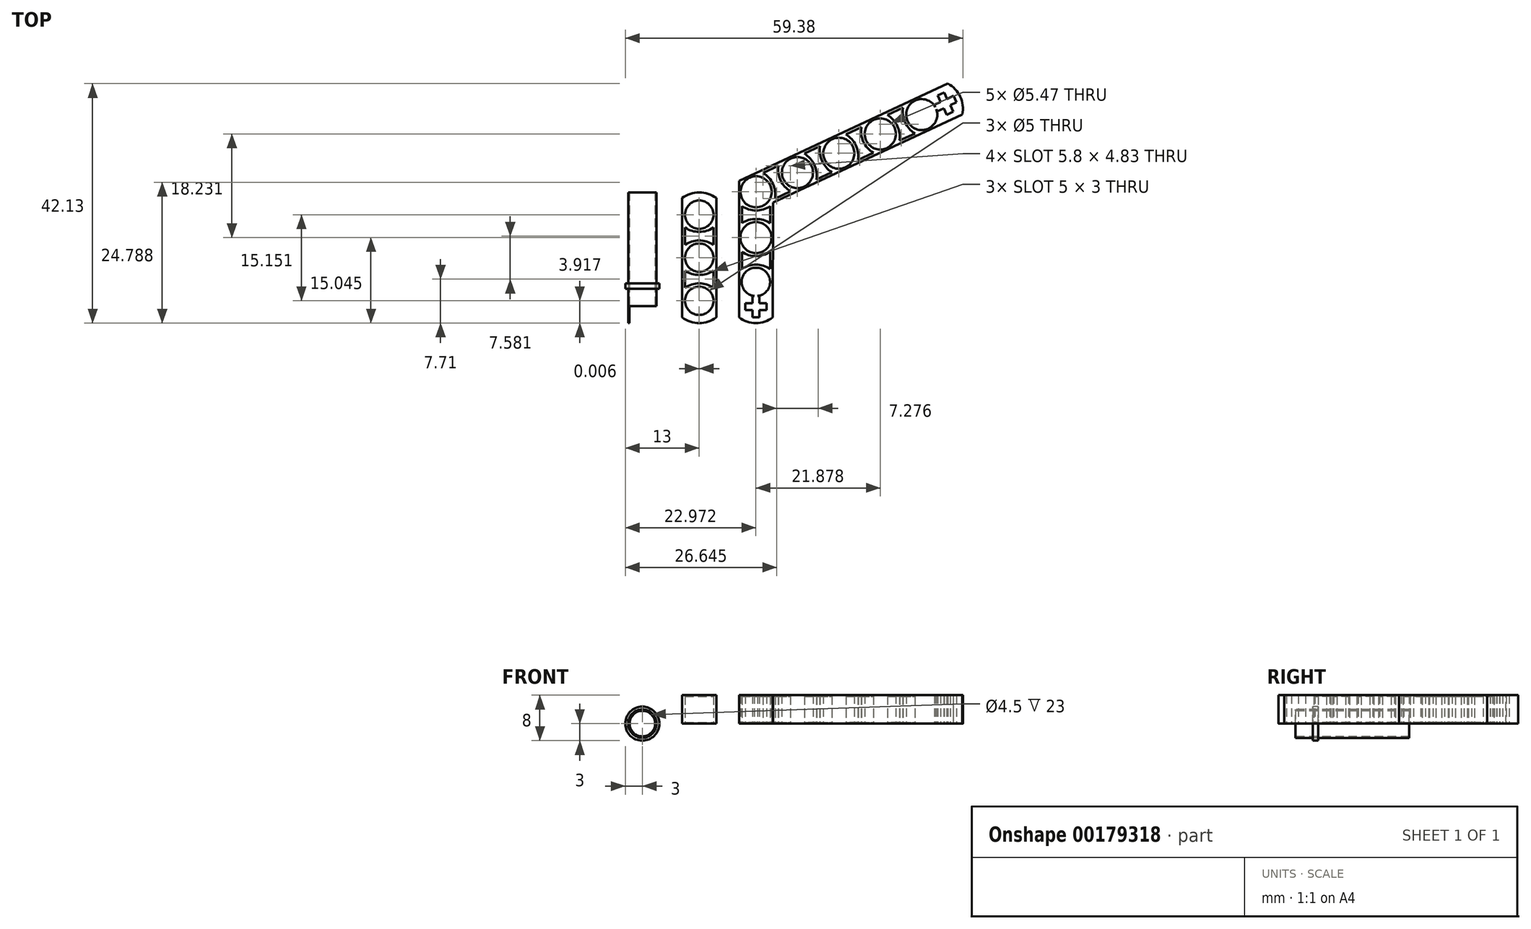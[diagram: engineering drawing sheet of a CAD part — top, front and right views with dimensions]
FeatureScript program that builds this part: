
annotation { "Feature Type Name" : "Feature", "Feature Type Description" : "" }
export const myFeature = defineFeature(function(context is Context, id is Id, definition is map)
    precondition{}
    {
        {
            var Q0;
            Q0=qCreatedBy(makeId("Top.planeOp"),FACE);
            var sketch = newSketch(context, id + "F0", { "sketchPlane" : qUnion([Q0])});
            skLineSegment(sketch, "E0", {"start": v(0, 1) * mm, "end": v(0, 23) * mm});
            skLineSegment(sketch, "E1", {"start": v(6, 22) * mm, "end": v(6, 1) * mm});
            skCircle(sketch, "E2", {"center": v(3, 11.5) * mm, "radius": 2.5 * mm});
            skLineSegment(sketch, "E3", {"start": v(0.5, 15.3) * mm, "end": v(0, 15.3) * mm, "construction": true});
            skLineSegment(sketch, "E4", {"start": v(3.02, 15.3) * mm, "end": v(6, 15.3) * mm, "construction": true});
            skLineSegment(sketch, "E5", {"start": v(0, 15.3) * mm, "end": v(0, 16.8) * mm, "construction": true});
            skLineSegment(sketch, "E6", {"start": v(0, 16.8) * mm, "end": v(0.5, 16.8) * mm, "construction": true});
            skLineSegment(sketch, "E7", {"start": v(0, 15.3) * mm, "end": v(0, 13.8) * mm, "construction": true});
            skLineSegment(sketch, "E8", {"start": v(0, 13.8) * mm, "end": v(0.5, 13.8) * mm, "construction": true});
            skLineSegment(sketch, "E9", {"start": v(6, 15.3) * mm, "end": v(6, 16.8) * mm});
            skLineSegment(sketch, "E10", {"start": v(6, 16.8) * mm, "end": v(5.5, 16.8) * mm, "construction": true});
            skLineSegment(sketch, "E11", {"start": v(6, 15.3) * mm, "end": v(6, 13.8) * mm, "construction": true});
            skLineSegment(sketch, "E12", {"start": v(6, 13.8) * mm, "end": v(5.5, 13.8) * mm, "construction": true});
            skLineSegment(sketch, "E13", {"start": v(6, 15.3) * mm, "end": v(6, 16.8) * mm, "construction": true});
            skLineSegment(sketch, "E14", {"start": v(0.5, 16.8) * mm, "end": v(0.5, 13.8) * mm});
            skLineSegment(sketch, "E15", {"start": v(5.5, 16.8) * mm, "end": v(5.5, 13.8) * mm});
            skLineSegment(sketch, "E16", {"start": v(6, 16.04) * mm, "end": v(0, 16.04) * mm, "construction": true});
            skLineSegment(sketch, "E17", {"start": v(6, 14.54) * mm, "end": v(0, 14.54) * mm, "construction": true});
            skArc(sketch, "E18", {"start": v(0.5, 16.8) * mm, "mid": v(3, 16.04) * mm, "end": v(5.5, 16.8) * mm});
            skArc(sketch, "E19", {"start": v(5.5, 13.8) * mm, "mid": v(3, 14.54) * mm, "end": v(0.5, 13.8) * mm});
            skPoint(sketch, "E20.endSnap0", {"position": v(3, 7.7) * mm});
            skLineSegment(sketch, "E21", {"start": v(3, 7.7) * mm, "end": v(6, 7.7) * mm, "construction": true});
            skLineSegment(sketch, "E22", {"start": v(0, 7.7) * mm, "end": v(0, 6.2) * mm, "construction": true});
            skLineSegment(sketch, "E23", {"start": v(0, 7.7) * mm, "end": v(0, 9.2) * mm, "construction": true});
            skLineSegment(sketch, "E24", {"start": v(6, 7.7) * mm, "end": v(6, 9.2) * mm, "construction": true});
            skLineSegment(sketch, "E25", {"start": v(6, 7.7) * mm, "end": v(6, 6.2) * mm, "construction": true});
            skLineSegment(sketch, "E26", {"start": v(6, 6.96) * mm, "end": v(0, 6.96) * mm, "construction": true});
            skLineSegment(sketch, "E27", {"start": v(0, 8.46) * mm, "end": v(6, 8.46) * mm, "construction": true});
            skLineSegment(sketch, "E28", {"start": v(6, 9.2) * mm, "end": v(5.5, 9.2) * mm, "construction": true});
            skLineSegment(sketch, "E29", {"start": v(0, 9.2) * mm, "end": v(0.5, 9.2) * mm, "construction": true});
            skLineSegment(sketch, "E30", {"start": v(0, 6.2) * mm, "end": v(0.5, 6.2) * mm, "construction": true});
            skLineSegment(sketch, "E31", {"start": v(6, 6.2) * mm, "end": v(5.5, 6.2) * mm, "construction": true});
            skArc(sketch, "E32", {"start": v(0.5, 9.2) * mm, "mid": v(3, 8.46) * mm, "end": v(5.5, 9.2) * mm});
            skArc(sketch, "E33", {"start": v(5.5, 6.2) * mm, "mid": v(3, 6.96) * mm, "end": v(0.5, 6.2) * mm});
            skLineSegment(sketch, "E34", {"start": v(5.5, 9.2) * mm, "end": v(5.5, 6.2) * mm});
            skLineSegment(sketch, "E35", {"start": v(0.5, 9.2) * mm, "end": v(0.5, 6.2) * mm});
            skLineSegment(sketch, "E36", {"start": v(3, 23) * mm, "end": v(3, 21) * mm, "construction": true});
            skLineSegment(sketch, "E37", {"start": v(3, 22) * mm, "end": v(6, 22) * mm, "construction": true});
            skLineSegment(sketch, "E38", {"start": v(3, 22) * mm, "end": v(0, 22) * mm, "construction": true});
            skArc(sketch, "E39", {"start": v(6, 22) * mm, "mid": v(3, 23) * mm, "end": v(0, 22) * mm});
            skPoint(sketch, "E40.orphan", {"position": v(6, 23) * mm});
            skLineSegment(sketch, "E41", {"start": v(3, 0) * mm, "end": v(3, 2) * mm, "construction": true});
            skLineSegment(sketch, "E42", {"start": v(3, 1) * mm, "end": v(6, 1) * mm, "construction": true});
            skLineSegment(sketch, "E43", {"start": v(3, 1) * mm, "end": v(0, 1) * mm, "construction": true});
            skArc(sketch, "E44", {"start": v(0, 1) * mm, "mid": v(3, 0) * mm, "end": v(6, 1) * mm});
            skPoint(sketch, "E45.orphan", {"position": v(6, 0) * mm});
            skPoint(sketch, "E46.orphan", {"position": v(0, 0) * mm});
            skLineSegment(sketch, "E47", {"start": v(3, 2) * mm, "end": v(3, 5) * mm, "construction": true});
            skCircle(sketch, "E48", {"center": v(3, 3.92) * mm, "radius": 2.5 * mm});
            skLineSegment(sketch, "E49", {"start": v(3, 6.42) * mm, "end": v(3, 9) * mm, "construction": true});
            skLineSegment(sketch, "E50", {"start": v(3, 7.7) * mm, "end": v(0, 7.7) * mm, "construction": true});
            skCircle(sketch, "E51", {"center": v(3, 19.07) * mm, "radius": 2.5 * mm});
            skLineSegment(sketch, "E52", {"start": v(3.02, 15.3) * mm, "end": v(3.02, 16.57) * mm, "construction": true});
            skLineSegment(sketch, "E53", {"start": v(3.02, 15.3) * mm, "end": v(3.02, 14) * mm, "construction": true});
            skLineSegment(sketch, "E54", {"start": v(3.02, 14) * mm, "end": v(3.02, 16.57) * mm, "construction": true});
            skPoint(sketch, "E55.start.orphan", {"position": v(3.02, 15.28) * mm});
            skLineSegment(sketch, "E56", {"start": v(3.02, 15.3) * mm, "end": v(0.5, 15.3) * mm, "construction": true});
            skLineSegment(sketch, "E57", {"start": v(0, 0) * mm, "end": v(-7, 0) * mm, "construction": true});
            skSolve(sketch);
        }
        {
            var Q0;
            Q0 = qSketchRegion(id + "F0", true);
            extrude(context, id + "F1", {"entities" : qUnion([Q0]), "depth" : 5 * mm});
        }
        {
            var Q0;
            Q0=makeQuery(id+"F0.imprint","IMPRINT",FACE,{"disambiguationData":[TD([[makeQuery(id+"F0.imprint","IMPRINT",EDGE,{"derivedFrom":sQuery(id+"F0.wireOp",EDGE,"E14")}),1.0]])]});
            var Q1;
            Q1=makeQuery(id+"F0.imprint","IMPRINT",FACE,{"disambiguationData":[TD([[makeQuery(id+"F0.imprint","IMPRINT",EDGE,{"derivedFrom":sQuery(id+"F0.wireOp",EDGE,"E32")}),-1.0]])]});
            extrude(context, id + "F2", {"entities" : qUnion([Q0, Q1]), "depth" : 5 * mm});
        }
        {
            var Q0;
            Q0=makeQuery(id+"F2.opExtrude","CAP_FACE",FACE,{"disambiguationData":[OSD([sQuery(id+"F0.wireOp",EDGE,"E14"),sQuery(id+"F0.wireOp",EDGE,"E15"),sQuery(id+"F0.wireOp",EDGE,"E18"),sQuery(id+"F0.wireOp",EDGE,"E19")])],"isStart":true});
            extrude(context, id + "F3", {"entities" : qUnion([Q0]), "operationType" : NewBodyOperationType.REMOVE, "oppositeDirection" : true, "depth" : 0.2 * mm});
        }
        {
            var Q0;
            Q0=makeQuery(id+"F2.opExtrude","CAP_FACE",FACE,{"disambiguationData":[OSD([sQuery(id+"F0.wireOp",EDGE,"E14"),sQuery(id+"F0.wireOp",EDGE,"E15"),sQuery(id+"F0.wireOp",EDGE,"E18"),sQuery(id+"F0.wireOp",EDGE,"E19")])],"isStart":false});
            extrude(context, id + "F4", {"entities" : qUnion([Q0]), "operationType" : NewBodyOperationType.REMOVE, "oppositeDirection" : true, "depth" : 0.2 * mm});
        }
        {
            var Q0;
            Q0=makeQuery(id+"F2.opExtrude","CAP_FACE",FACE,{"disambiguationData":[OSD([sQuery(id+"F0.wireOp",EDGE,"E32"),sQuery(id+"F0.wireOp",EDGE,"E33"),sQuery(id+"F0.wireOp",EDGE,"E34"),sQuery(id+"F0.wireOp",EDGE,"E35")])],"isStart":true});
            extrude(context, id + "F5", {"entities" : qUnion([Q0]), "operationType" : NewBodyOperationType.REMOVE, "oppositeDirection" : true, "depth" : 0.2 * mm});
        }
        {
            var Q0;
            Q0=makeQuery(id+"F2.opExtrude","CAP_FACE",FACE,{"disambiguationData":[OSD([sQuery(id+"F0.wireOp",EDGE,"E32"),sQuery(id+"F0.wireOp",EDGE,"E33"),sQuery(id+"F0.wireOp",EDGE,"E34"),sQuery(id+"F0.wireOp",EDGE,"E35")])],"isStart":false});
            extrude(context, id + "F6", {"entities" : qUnion([Q0]), "operationType" : NewBodyOperationType.REMOVE, "oppositeDirection" : true, "depth" : 0.2 * mm});
        }
        {
            var Q0;
            Q0=qCreatedBy(makeId("Top.planeOp"),FACE);
            var sketch = newSketch(context, id + "F7", { "sketchPlane" : qUnion([Q0])});
            skLineSegment(sketch, "E58", {"start": v(0, 0) * mm, "end": v(10, 0) * mm, "construction": true});
            skLineSegment(sketch, "E59", {"start": v(10, 1) * mm, "end": v(10, 25) * mm});
            skLineSegment(sketch, "E60", {"start": v(10, 25) * mm, "end": v(46.74, 42.13) * mm});
            skLineSegment(sketch, "E61", {"start": v(10, 25) * mm, "end": v(16, 21.18) * mm, "construction": true});
            skLineSegment(sketch, "E62", {"start": v(10, 21.18) * mm, "end": v(16, 21.18) * mm, "construction": true});
            skLineSegment(sketch, "E63", {"start": v(49.28, 36.7) * mm, "end": v(16, 21.18) * mm});
            skLineSegment(sketch, "E64", {"start": v(15.95, 1) * mm, "end": v(16, 21.18) * mm});
            skCircle(sketch, "E65", {"center": v(13, 23.09) * mm, "radius": 2.73 * mm});
            skLineSegment(sketch, "E66", {"start": v(12.97, 1) * mm, "end": v(12.97, 9.74) * mm, "construction": true});
            skLineSegment(sketch, "E67", {"start": v(12.97, 5.09) * mm, "end": v(12.97, 7.24) * mm, "construction": true});
            skCircle(sketch, "E68", {"center": v(12.97, 7.24) * mm, "radius": 2.5 * mm});
            skLineSegment(sketch, "E69", {"start": v(20.29, 26.49) * mm, "end": v(20.29, 26.5) * mm, "construction": true});
            skArc(sketch, "E70", {"start": v(20.29, 26.49) * mm, "mid": v(20.29, 26.49) * mm, "end": v(20.29, 26.5) * mm});
            skArc(sketch, "E71", {"start": v(10, 1) * mm, "mid": v(12.97, 0) * mm, "end": v(15.95, 1) * mm});
            skPoint(sketch, "E72.start.orphan", {"position": v(15.94, 0) * mm});
            skLineSegment(sketch, "E73", {"start": v(12.35, 1) * mm, "end": v(12.97, 1) * mm, "construction": true});
            skLineSegment(sketch, "E74", {"start": v(12.97, 1) * mm, "end": v(12.35, 1) * mm});
            skLineSegment(sketch, "E75", {"start": v(12.97, 1) * mm, "end": v(13.6, 1) * mm});
            skLineSegment(sketch, "E76", {"start": v(13.6, 1) * mm, "end": v(13.6, 2.25) * mm});
            skLineSegment(sketch, "E77", {"start": v(13.6, 2.25) * mm, "end": v(14.85, 2.25) * mm});
            skLineSegment(sketch, "E78", {"start": v(14.85, 2.25) * mm, "end": v(14.85, 3.5) * mm});
            skLineSegment(sketch, "E79", {"start": v(14.85, 3.5) * mm, "end": v(13.6, 3.5) * mm});
            skLineSegment(sketch, "E80", {"start": v(12.35, 2.25) * mm, "end": v(12.35, 1) * mm});
            skLineSegment(sketch, "E81", {"start": v(13.6, 3.5) * mm, "end": v(13.6, 4.75) * mm});
            skLineSegment(sketch, "E82", {"start": v(13.6, 4.75) * mm, "end": v(12.35, 4.75) * mm});
            skLineSegment(sketch, "E83", {"start": v(12.35, 4.75) * mm, "end": v(12.35, 3.5) * mm});
            skLineSegment(sketch, "E84", {"start": v(12.35, 3.5) * mm, "end": v(11.1, 3.5) * mm});
            skLineSegment(sketch, "E85", {"start": v(11.1, 3.5) * mm, "end": v(11.1, 2.25) * mm});
            skLineSegment(sketch, "E86", {"start": v(11.1, 2.25) * mm, "end": v(12.35, 2.25) * mm});
            skLineSegment(sketch, "E87.trimOffspring", {"start": v(12.97, 18.35) * mm, "end": v(12.97, 18.35) * mm, "construction": true});
            skPoint(sketch, "E88.orphan", {"position": v(12.97, 20.36) * mm});
            skPoint(sketch, "E89.orphan", {"position": v(12.97, 10.18) * mm});
            skLineSegment(sketch, "E90", {"start": v(12.97, 15.05) * mm, "end": v(10, 15.05) * mm, "construction": true});
            skLineSegment(sketch, "E91", {"start": v(12.97, 15.05) * mm, "end": v(15.98, 15.05) * mm, "construction": true});
            skCircle(sketch, "E92", {"center": v(12.97, 15.05) * mm, "radius": 2.73 * mm});
            skLineSegment(sketch, "E93.trimOffspring", {"start": v(12.97, 12.31) * mm, "end": v(12.97, 17.78) * mm, "construction": true});
            skLineSegment(sketch, "E94", {"start": v(12.97, 12.31) * mm, "end": v(12.97, 9.74) * mm, "construction": true});
            skLineSegment(sketch, "E95", {"start": v(12.97, 20.36) * mm, "end": v(12.97, 17.78) * mm, "construction": true});
            skLineSegment(sketch, "E96", {"start": v(17.81, 25.33) * mm, "end": v(15.48, 24.24) * mm, "construction": true});
            skCircle(sketch, "E97", {"center": v(20.28, 26.48) * mm, "radius": 2.73 * mm});
            skLineSegment(sketch, "E98", {"start": v(25.09, 28.73) * mm, "end": v(22.75, 27.64) * mm, "construction": true});
            skCircle(sketch, "E99", {"center": v(27.56, 29.88) * mm, "radius": 2.73 * mm});
            skLineSegment(sketch, "E100", {"start": v(32.39, 32.13) * mm, "end": v(30.05, 31.04) * mm, "construction": true});
            skCircle(sketch, "E101", {"center": v(34.85, 33.28) * mm, "radius": 2.73 * mm});
            skLineSegment(sketch, "E102", {"start": v(39.7, 35.53) * mm, "end": v(37.35, 34.46) * mm, "construction": true});
            skCircle(sketch, "E103", {"center": v(42.14, 36.68) * mm, "radius": 2.73 * mm});
            skLineSegment(sketch, "E104", {"start": v(48.01, 38.72) * mm, "end": v(48.01, 38.73) * mm});
            skLineSegment(sketch, "E105", {"start": v(47.48, 39.86) * mm, "end": v(47.75, 39.98) * mm});
            skLineSegment(sketch, "E106", {"start": v(48.01, 39.41) * mm, "end": v(48.27, 38.85) * mm, "construction": true});
            skLineSegment(sketch, "E107", {"start": v(48.01, 39.41) * mm, "end": v(47.75, 39.98) * mm});
            skLineSegment(sketch, "E108", {"start": v(48.01, 39.41) * mm, "end": v(48.27, 38.85) * mm});
            skLineSegment(sketch, "E109", {"start": v(48.27, 38.85) * mm, "end": v(47.14, 38.32) * mm});
            skPoint(sketch, "E110.end.orphan", {"position": v(48.01, 37.42) * mm});
            skLineSegment(sketch, "E111", {"start": v(47.14, 38.32) * mm, "end": v(47.67, 37.19) * mm});
            skLineSegment(sketch, "E112", {"start": v(47.67, 37.19) * mm, "end": v(46.54, 36.66) * mm});
            skLineSegment(sketch, "E113", {"start": v(46.54, 36.66) * mm, "end": v(46, 37.8) * mm});
            skLineSegment(sketch, "E114", {"start": v(46, 37.8) * mm, "end": v(44.88, 37.26) * mm});
            skLineSegment(sketch, "E115", {"start": v(44.88, 37.26) * mm, "end": v(44.35, 38.4) * mm});
            skLineSegment(sketch, "E116", {"start": v(44.35, 38.4) * mm, "end": v(45.48, 38.92) * mm});
            skLineSegment(sketch, "E117", {"start": v(45.48, 38.92) * mm, "end": v(44.95, 40.06) * mm});
            skLineSegment(sketch, "E118", {"start": v(44.95, 40.06) * mm, "end": v(46.09, 40.59) * mm});
            skLineSegment(sketch, "E119", {"start": v(46.09, 40.59) * mm, "end": v(46.61, 39.45) * mm});
            skLineSegment(sketch, "E120", {"start": v(46.61, 39.45) * mm, "end": v(47.75, 39.98) * mm});
            skPoint(sketch, "E121.orphan", {"position": v(12.97, 0) * mm});
            skLineSegment(sketch, "E122", {"start": v(12.97, 1) * mm, "end": v(12.97, 0) * mm, "construction": true});
            skLineSegment(sketch, "E123.trimOffspring", {"start": v(48.01, 39.41) * mm, "end": v(15.48, 24.24) * mm, "construction": true});
            skLineSegment(sketch, "E124", {"start": v(48.01, 39.41) * mm, "end": v(48.91, 39.85) * mm, "construction": true});
            skLineSegment(sketch, "E125", {"start": v(47.75, 39.98) * mm, "end": v(46.74, 42.13) * mm, "construction": true});
            skLineSegment(sketch, "E126", {"start": v(48.27, 38.85) * mm, "end": v(49.28, 36.7) * mm, "construction": true});
            skArc(sketch, "E127", {"start": v(49.28, 36.7) * mm, "mid": v(48.92, 39.84) * mm, "end": v(46.74, 42.13) * mm});
            skLineSegment(sketch, "E128", {"start": v(12.97, 11.02) * mm, "end": v(10, 11.02) * mm, "construction": true});
            skLineSegment(sketch, "E129", {"start": v(12.97, 11.02) * mm, "end": v(15.97, 11.02) * mm, "construction": true});
            skLineSegment(sketch, "E130", {"start": v(15.97, 11.02) * mm, "end": v(15.98, 12.52) * mm, "construction": true});
            skLineSegment(sketch, "E131", {"start": v(15.97, 11.02) * mm, "end": v(15.97, 9.52) * mm, "construction": true});
            skLineSegment(sketch, "E132", {"start": v(10, 11.02) * mm, "end": v(10, 12.52) * mm, "construction": true});
            skLineSegment(sketch, "E133", {"start": v(10, 11.02) * mm, "end": v(10, 9.52) * mm, "construction": true});
            skLineSegment(sketch, "E134", {"start": v(10, 9.52) * mm, "end": v(10.5, 9.52) * mm, "construction": true});
            skLineSegment(sketch, "E135", {"start": v(10, 12.52) * mm, "end": v(10.5, 12.52) * mm, "construction": true});
            skLineSegment(sketch, "E136", {"start": v(15.98, 12.52) * mm, "end": v(15.48, 12.53) * mm, "construction": true});
            skLineSegment(sketch, "E137", {"start": v(15.97, 9.52) * mm, "end": v(15.47, 9.53) * mm, "construction": true});
            skLineSegment(sketch, "E138", {"start": v(10, 11.77) * mm, "end": v(15.98, 11.77) * mm, "construction": true});
            skLineSegment(sketch, "E139", {"start": v(10, 10.27) * mm, "end": v(15.97, 10.26) * mm, "construction": true});
            skPoint(sketch, "E139.endSnap0", {"position": v(15.97, 10.27) * mm});
            skLineSegment(sketch, "E140", {"start": v(10.5, 12.52) * mm, "end": v(10.5, 9.52) * mm});
            skLineSegment(sketch, "E141", {"start": v(15.48, 12.53) * mm, "end": v(15.47, 9.53) * mm});
            skArc(sketch, "E142", {"start": v(10.5, 12.52) * mm, "mid": v(12.99, 11.77) * mm, "end": v(15.48, 12.53) * mm});
            skArc(sketch, "E143", {"start": v(15.47, 9.53) * mm, "mid": v(12.98, 10.27) * mm, "end": v(10.5, 9.52) * mm});
            skLineSegment(sketch, "E144", {"start": v(12.97, 19.07) * mm, "end": v(10, 19.07) * mm, "construction": true});
            skLineSegment(sketch, "E145", {"start": v(10, 19.07) * mm, "end": v(10, 20.57) * mm, "construction": true});
            skLineSegment(sketch, "E146", {"start": v(10, 20.57) * mm, "end": v(10.5, 20.57) * mm, "construction": true});
            skLineSegment(sketch, "E147", {"start": v(10, 19.07) * mm, "end": v(10, 17.57) * mm, "construction": true});
            skLineSegment(sketch, "E148", {"start": v(10, 17.57) * mm, "end": v(10.5, 17.57) * mm, "construction": true});
            skLineSegment(sketch, "E149", {"start": v(12.97, 19.07) * mm, "end": v(16, 19.07) * mm, "construction": true});
            skLineSegment(sketch, "E150", {"start": v(16, 19.07) * mm, "end": v(16, 20.57) * mm, "construction": true});
            skLineSegment(sketch, "E151", {"start": v(16, 20.57) * mm, "end": v(15.5, 20.57) * mm, "construction": true});
            skLineSegment(sketch, "E152", {"start": v(16, 19.07) * mm, "end": v(16, 17.57) * mm, "construction": true});
            skLineSegment(sketch, "E153", {"start": v(16, 17.57) * mm, "end": v(15.5, 17.57) * mm, "construction": true});
            skLineSegment(sketch, "E154", {"start": v(10, 19.82) * mm, "end": v(16, 19.82) * mm, "construction": true});
            skLineSegment(sketch, "E155", {"start": v(10, 18.32) * mm, "end": v(16, 18.3) * mm, "construction": true});
            skArc(sketch, "E156", {"start": v(10.5, 20.57) * mm, "mid": v(13, 19.81) * mm, "end": v(15.5, 20.57) * mm});
            skArc(sketch, "E157", {"start": v(15.5, 17.57) * mm, "mid": v(13, 18.3) * mm, "end": v(10.5, 17.57) * mm});
            skLineSegment(sketch, "E158", {"start": v(10.5, 20.57) * mm, "end": v(10.5, 17.57) * mm});
            skLineSegment(sketch, "E159", {"start": v(15.5, 20.57) * mm, "end": v(15.5, 17.57) * mm});
            skLineSegment(sketch, "E160", {"start": v(16.64, 24.79) * mm, "end": v(17.91, 22.07) * mm, "construction": true});
            skLineSegment(sketch, "E161", {"start": v(16.64, 24.79) * mm, "end": v(15.38, 27.5) * mm, "construction": true});
            skLineSegment(sketch, "E162", {"start": v(15.38, 27.5) * mm, "end": v(14.02, 26.87) * mm, "construction": true});
            skLineSegment(sketch, "E163", {"start": v(15.38, 27.5) * mm, "end": v(16.74, 28.14) * mm, "construction": true});
            skLineSegment(sketch, "E164", {"start": v(17.91, 22.07) * mm, "end": v(16.55, 21.44) * mm, "construction": true});
            skLineSegment(sketch, "E165", {"start": v(17.91, 22.07) * mm, "end": v(19.27, 22.7) * mm, "construction": true});
            skLineSegment(sketch, "E166", {"start": v(14.02, 26.87) * mm, "end": v(14.23, 26.42) * mm, "construction": true});
            skLineSegment(sketch, "E167", {"start": v(16.74, 28.14) * mm, "end": v(16.95, 27.69) * mm, "construction": true});
            skLineSegment(sketch, "E168", {"start": v(16.55, 21.44) * mm, "end": v(16.34, 21.89) * mm, "construction": true});
            skLineSegment(sketch, "E169", {"start": v(19.27, 22.7) * mm, "end": v(19.06, 23.16) * mm, "construction": true});
            skLineSegment(sketch, "E170", {"start": v(14.7, 27.2) * mm, "end": v(17.23, 21.75) * mm, "construction": true});
            skLineSegment(sketch, "E171", {"start": v(16.06, 27.82) * mm, "end": v(18.6, 22.39) * mm, "construction": true});
            skArc(sketch, "E172", {"start": v(16.34, 21.89) * mm, "mid": v(15.97, 24.47) * mm, "end": v(14.23, 26.42) * mm});
            skArc(sketch, "E173", {"start": v(16.95, 27.69) * mm, "mid": v(17.32, 25.1) * mm, "end": v(19.06, 23.16) * mm});
            skLineSegment(sketch, "E174", {"start": v(14.23, 26.42) * mm, "end": v(16.95, 27.69) * mm});
            skLineSegment(sketch, "E175", {"start": v(16.34, 21.89) * mm, "end": v(19.06, 23.16) * mm});
            skLineSegment(sketch, "E176", {"start": v(23.92, 28.18) * mm, "end": v(22.65, 30.9) * mm, "construction": true});
            skLineSegment(sketch, "E177", {"start": v(23.92, 28.18) * mm, "end": v(25.19, 25.46) * mm, "construction": true});
            skLineSegment(sketch, "E178", {"start": v(22.65, 30.9) * mm, "end": v(21.3, 30.27) * mm, "construction": true});
            skLineSegment(sketch, "E179", {"start": v(21.3, 30.27) * mm, "end": v(21.5, 29.81) * mm, "construction": true});
            skLineSegment(sketch, "E180", {"start": v(22.65, 30.9) * mm, "end": v(24.01, 31.53) * mm, "construction": true});
            skLineSegment(sketch, "E181", {"start": v(24.01, 31.53) * mm, "end": v(24.22, 31.08) * mm, "construction": true});
            skLineSegment(sketch, "E182", {"start": v(25.19, 25.46) * mm, "end": v(23.83, 24.83) * mm, "construction": true});
            skLineSegment(sketch, "E183", {"start": v(23.83, 24.83) * mm, "end": v(23.62, 25.28) * mm, "construction": true});
            skLineSegment(sketch, "E184", {"start": v(25.19, 25.46) * mm, "end": v(26.55, 26.1) * mm, "construction": true});
            skLineSegment(sketch, "E185", {"start": v(26.55, 26.1) * mm, "end": v(26.34, 26.55) * mm, "construction": true});
            skLineSegment(sketch, "E186", {"start": v(24.5, 25.15) * mm, "end": v(21.97, 30.58) * mm, "construction": true});
            skLineSegment(sketch, "E187", {"start": v(23.33, 31.22) * mm, "end": v(25.87, 25.78) * mm, "construction": true});
            skArc(sketch, "E188", {"start": v(23.62, 25.28) * mm, "mid": v(23.24, 27.87) * mm, "end": v(21.5, 29.81) * mm});
            skArc(sketch, "E189", {"start": v(24.22, 31.08) * mm, "mid": v(24.6, 28.5) * mm, "end": v(26.34, 26.55) * mm});
            skLineSegment(sketch, "E190", {"start": v(21.5, 29.81) * mm, "end": v(24.22, 31.08) * mm});
            skLineSegment(sketch, "E191", {"start": v(23.62, 25.28) * mm, "end": v(26.34, 26.55) * mm});
            skLineSegment(sketch, "E192", {"start": v(31.22, 31.58) * mm, "end": v(29.95, 34.3) * mm, "construction": true});
            skLineSegment(sketch, "E193", {"start": v(29.95, 34.3) * mm, "end": v(28.6, 33.67) * mm, "construction": true});
            skLineSegment(sketch, "E194", {"start": v(28.6, 33.67) * mm, "end": v(28.8, 33.22) * mm, "construction": true});
            skLineSegment(sketch, "E195", {"start": v(31.22, 31.58) * mm, "end": v(32.48, 28.87) * mm, "construction": true});
            skLineSegment(sketch, "E196", {"start": v(32.48, 28.87) * mm, "end": v(33.84, 29.5) * mm, "construction": true});
            skLineSegment(sketch, "E197", {"start": v(33.84, 29.5) * mm, "end": v(33.63, 29.95) * mm, "construction": true});
            skLineSegment(sketch, "E198", {"start": v(29.95, 34.3) * mm, "end": v(31.3, 34.94) * mm, "construction": true});
            skLineSegment(sketch, "E199", {"start": v(31.3, 34.94) * mm, "end": v(31.52, 34.48) * mm, "construction": true});
            skLineSegment(sketch, "E200", {"start": v(32.48, 28.87) * mm, "end": v(31.13, 28.23) * mm, "construction": true});
            skLineSegment(sketch, "E201", {"start": v(31.13, 28.23) * mm, "end": v(30.91, 28.69) * mm, "construction": true});
            skLineSegment(sketch, "E202", {"start": v(31.8, 28.55) * mm, "end": v(29.27, 33.99) * mm, "construction": true});
            skLineSegment(sketch, "E203", {"start": v(30.63, 34.62) * mm, "end": v(33.16, 29.18) * mm, "construction": true});
            skArc(sketch, "E204", {"start": v(30.91, 28.69) * mm, "mid": v(30.54, 31.27) * mm, "end": v(28.8, 33.22) * mm});
            skArc(sketch, "E205", {"start": v(31.52, 34.48) * mm, "mid": v(31.9, 31.9) * mm, "end": v(33.63, 29.95) * mm});
            skLineSegment(sketch, "E206", {"start": v(28.8, 33.22) * mm, "end": v(31.52, 34.48) * mm});
            skLineSegment(sketch, "E207", {"start": v(30.91, 28.69) * mm, "end": v(33.63, 29.95) * mm});
            skLineSegment(sketch, "E208", {"start": v(38.53, 35) * mm, "end": v(37.26, 37.71) * mm, "construction": true});
            skLineSegment(sketch, "E209", {"start": v(38.53, 35) * mm, "end": v(39.8, 32.28) * mm, "construction": true});
            skLineSegment(sketch, "E210", {"start": v(41.15, 32.9) * mm, "end": v(40.94, 33.36) * mm});
            skLineSegment(sketch, "E211", {"start": v(37.26, 37.71) * mm, "end": v(35.9, 37.08) * mm, "construction": true});
            skLineSegment(sketch, "E212", {"start": v(35.9, 37.08) * mm, "end": v(36.11, 36.62) * mm, "construction": true});
            skLineSegment(sketch, "E213", {"start": v(37.26, 37.71) * mm, "end": v(38.62, 38.34) * mm, "construction": true});
            skLineSegment(sketch, "E214", {"start": v(38.62, 38.34) * mm, "end": v(38.83, 37.9) * mm, "construction": true});
            skLineSegment(sketch, "E215", {"start": v(39.8, 32.28) * mm, "end": v(41.15, 32.9) * mm, "construction": true});
            skLineSegment(sketch, "E216", {"start": v(37.94, 38.03) * mm, "end": v(40.47, 32.6) * mm, "construction": true});
            skPoint(sketch, "E216.endSnap0", {"position": v(40.47, 32.6) * mm});
            skLineSegment(sketch, "E217", {"start": v(36.58, 37.4) * mm, "end": v(39.11, 31.96) * mm, "construction": true});
            skLineSegment(sketch, "E218", {"start": v(38.43, 31.64) * mm, "end": v(38.22, 32.1) * mm, "construction": true});
            skLineSegment(sketch, "E219.trimOffspring", {"start": v(38.22, 32.1) * mm, "end": v(38.43, 31.64) * mm, "construction": true});
            skLineSegment(sketch, "E220", {"start": v(36.11, 36.62) * mm, "end": v(38.83, 37.9) * mm});
            skLineSegment(sketch, "E221", {"start": v(38.22, 32.1) * mm, "end": v(40.94, 33.36) * mm});
            skArc(sketch, "E222", {"start": v(38.22, 32.1) * mm, "mid": v(37.85, 34.68) * mm, "end": v(36.11, 36.62) * mm});
            skArc(sketch, "E223", {"start": v(38.83, 37.9) * mm, "mid": v(39.2, 35.3) * mm, "end": v(40.94, 33.36) * mm});
            skSolve(sketch);
        }
        {
            var Q0;
            Q0=makeQuery(id+"F7.imprint","IMPRINT",FACE,{"disambiguationData":[TD([[makeQuery(id+"F7.imprint","IMPRINT",EDGE,{"derivedFrom":sQuery(id+"F7.wireOp",EDGE,"E59")}),-1.0]])]});
            extrude(context, id + "F8", {"entities" : qUnion([Q0]), "depth" : 5 * mm});
        }
        {
            var Q0;
            Q0=makeQuery(id+"F7.imprint","IMPRINT",FACE,{"disambiguationData":[TD([[makeQuery(id+"F7.imprint","IMPRINT",EDGE,{"derivedFrom":sQuery(id+"F7.wireOp",EDGE,"E140")}),1.0]])]});
            var Q1;
            Q1=makeQuery(id+"F7.imprint","IMPRINT",FACE,{"disambiguationData":[TD([[makeQuery(id+"F7.imprint","IMPRINT",EDGE,{"derivedFrom":sQuery(id+"F7.wireOp",EDGE,"E156")}),-1.0]])]});
            var Q2;
            Q2=makeQuery(id+"F7.imprint","IMPRINT",FACE,{"disambiguationData":[TD([[makeQuery(id+"F7.imprint","IMPRINT",EDGE,{"derivedFrom":sQuery(id+"F7.wireOp",EDGE,"E172")}),-1.0]])]});
            var Q3;
            Q3=makeQuery(id+"F7.imprint","IMPRINT",FACE,{"disambiguationData":[TD([[makeQuery(id+"F7.imprint","IMPRINT",EDGE,{"derivedFrom":sQuery(id+"F7.wireOp",EDGE,"E188")}),-1.0]])]});
            var Q4;
            Q4=makeQuery(id+"F7.imprint","IMPRINT",FACE,{"disambiguationData":[TD([[makeQuery(id+"F7.imprint","IMPRINT",EDGE,{"derivedFrom":sQuery(id+"F7.wireOp",EDGE,"E204")}),-1.0]])]});
            var Q5;
            Q5=makeQuery(id+"F7.imprint","IMPRINT",FACE,{"disambiguationData":[TD([[makeQuery(id+"F7.imprint","IMPRINT",EDGE,{"derivedFrom":sQuery(id+"F7.wireOp",EDGE,"E220")}),-1.0]])]});
            extrude(context, id + "F9", {"entities" : qUnion([Q0, Q1, Q2, Q3, Q4, Q5]), "depth" : 5 * mm});
        }
        {
            var Q0;
            Q0=makeQuery(id+"F9.opExtrude","CAP_FACE",FACE,{"disambiguationData":[OSD([sQuery(id+"F7.wireOp",EDGE,"E140"),sQuery(id+"F7.wireOp",EDGE,"E141"),sQuery(id+"F7.wireOp",EDGE,"E142"),sQuery(id+"F7.wireOp",EDGE,"E143")])],"isStart":false});
            extrude(context, id + "F10", {"entities" : qUnion([Q0]), "operationType" : NewBodyOperationType.REMOVE, "oppositeDirection" : true, "depth" : 0.2 * mm});
        }
        {
            var Q0;
            Q0=makeQuery(id+"F9.opExtrude","CAP_FACE",FACE,{"disambiguationData":[OSD([sQuery(id+"F7.wireOp",EDGE,"E140"),sQuery(id+"F7.wireOp",EDGE,"E141"),sQuery(id+"F7.wireOp",EDGE,"E142"),sQuery(id+"F7.wireOp",EDGE,"E143")])],"isStart":true});
            extrude(context, id + "F11", {"entities" : qUnion([Q0]), "operationType" : NewBodyOperationType.REMOVE, "oppositeDirection" : true, "depth" : 0.2 * mm});
        }
        {
            var Q0;
            Q0=makeQuery(id+"F9.opExtrude","CAP_FACE",FACE,{"disambiguationData":[OSD([sQuery(id+"F7.wireOp",EDGE,"E156"),sQuery(id+"F7.wireOp",EDGE,"E157"),sQuery(id+"F7.wireOp",EDGE,"E158"),sQuery(id+"F7.wireOp",EDGE,"E159")])],"isStart":false});
            extrude(context, id + "F12", {"entities" : qUnion([Q0]), "operationType" : NewBodyOperationType.REMOVE, "oppositeDirection" : true, "depth" : 0.2 * mm});
        }
        {
            var Q0;
            Q0=makeQuery(id+"F9.opExtrude","CAP_FACE",FACE,{"disambiguationData":[OSD([sQuery(id+"F7.wireOp",EDGE,"E156"),sQuery(id+"F7.wireOp",EDGE,"E157"),sQuery(id+"F7.wireOp",EDGE,"E158"),sQuery(id+"F7.wireOp",EDGE,"E159")])],"isStart":true});
            extrude(context, id + "F13", {"entities" : qUnion([Q0]), "operationType" : NewBodyOperationType.REMOVE, "oppositeDirection" : true, "depth" : 0.2 * mm});
        }
        {
            var Q0;
            Q0=makeQuery(id+"F9.opExtrude","CAP_FACE",FACE,{"disambiguationData":[OSD([sQuery(id+"F7.wireOp",EDGE,"E172"),sQuery(id+"F7.wireOp",EDGE,"E173"),sQuery(id+"F7.wireOp",EDGE,"E174"),sQuery(id+"F7.wireOp",EDGE,"E175")])],"isStart":false});
            extrude(context, id + "F14", {"entities" : qUnion([Q0]), "operationType" : NewBodyOperationType.REMOVE, "oppositeDirection" : true, "depth" : 0.2 * mm});
        }
        {
            var Q0;
            Q0=makeQuery(id+"F9.opExtrude","CAP_FACE",FACE,{"disambiguationData":[OSD([sQuery(id+"F7.wireOp",EDGE,"E172"),sQuery(id+"F7.wireOp",EDGE,"E173"),sQuery(id+"F7.wireOp",EDGE,"E174"),sQuery(id+"F7.wireOp",EDGE,"E175")])],"isStart":true});
            extrude(context, id + "F15", {"entities" : qUnion([Q0]), "operationType" : NewBodyOperationType.REMOVE, "oppositeDirection" : true, "depth" : 0.2 * mm});
        }
        {
            var Q0;
            Q0=makeQuery(id+"F9.opExtrude","CAP_FACE",FACE,{"disambiguationData":[OSD([sQuery(id+"F7.wireOp",EDGE,"E188"),sQuery(id+"F7.wireOp",EDGE,"E189"),sQuery(id+"F7.wireOp",EDGE,"E190"),sQuery(id+"F7.wireOp",EDGE,"E191")])],"isStart":false});
            extrude(context, id + "F16", {"entities" : qUnion([Q0]), "operationType" : NewBodyOperationType.REMOVE, "oppositeDirection" : true, "depth" : 0.2 * mm});
        }
        {
            var Q0;
            Q0=makeQuery(id+"F9.opExtrude","CAP_FACE",FACE,{"disambiguationData":[OSD([sQuery(id+"F7.wireOp",EDGE,"E188"),sQuery(id+"F7.wireOp",EDGE,"E189"),sQuery(id+"F7.wireOp",EDGE,"E190"),sQuery(id+"F7.wireOp",EDGE,"E191")])],"isStart":true});
            extrude(context, id + "F17", {"entities" : qUnion([Q0]), "operationType" : NewBodyOperationType.REMOVE, "oppositeDirection" : true, "depth" : 0.2 * mm});
        }
        {
            var Q0;
            Q0=makeQuery(id+"F9.opExtrude","CAP_FACE",FACE,{"disambiguationData":[OSD([sQuery(id+"F7.wireOp",EDGE,"E204"),sQuery(id+"F7.wireOp",EDGE,"E205"),sQuery(id+"F7.wireOp",EDGE,"E206"),sQuery(id+"F7.wireOp",EDGE,"E207")])],"isStart":false});
            extrude(context, id + "F18", {"entities" : qUnion([Q0]), "operationType" : NewBodyOperationType.REMOVE, "oppositeDirection" : true, "depth" : 0.2 * mm});
        }
        {
            var Q0;
            Q0=makeQuery(id+"F9.opExtrude","CAP_FACE",FACE,{"disambiguationData":[OSD([sQuery(id+"F7.wireOp",EDGE,"E204"),sQuery(id+"F7.wireOp",EDGE,"E205"),sQuery(id+"F7.wireOp",EDGE,"E206"),sQuery(id+"F7.wireOp",EDGE,"E207")])],"isStart":true});
            extrude(context, id + "F19", {"entities" : qUnion([Q0]), "operationType" : NewBodyOperationType.REMOVE, "oppositeDirection" : true, "depth" : 0.2 * mm});
        }
        {
            var Q0;
            Q0=makeQuery(id+"F9.opExtrude","CAP_FACE",FACE,{"disambiguationData":[OSD([sQuery(id+"F7.wireOp",EDGE,"E220"),sQuery(id+"F7.wireOp",EDGE,"E221"),sQuery(id+"F7.wireOp",EDGE,"E222"),sQuery(id+"F7.wireOp",EDGE,"E223")])],"isStart":false});
            extrude(context, id + "F20", {"entities" : qUnion([Q0]), "operationType" : NewBodyOperationType.REMOVE, "oppositeDirection" : true, "depth" : 0.2 * mm});
        }
        {
            var Q0;
            Q0=makeQuery(id+"F9.opExtrude","CAP_FACE",FACE,{"disambiguationData":[OSD([sQuery(id+"F7.wireOp",EDGE,"E220"),sQuery(id+"F7.wireOp",EDGE,"E221"),sQuery(id+"F7.wireOp",EDGE,"E222"),sQuery(id+"F7.wireOp",EDGE,"E223")])],"isStart":true});
            extrude(context, id + "F21", {"entities" : qUnion([Q0]), "operationType" : NewBodyOperationType.REMOVE, "oppositeDirection" : true, "depth" : 0.2 * mm});
        }
        {
            var Q0;
            Q0=qCreatedBy(makeId("Front.planeOp"),FACE);
            var sketch = newSketch(context, id + "F22", { "sketchPlane" : qUnion([Q0])});
            skLineSegment(sketch, "E224", {"start": v(0, 0) * mm, "end": v(-7, 0) * mm, "construction": true});
            skCircle(sketch, "E225", {"center": v(-7, 0) * mm, "radius": 2.5 * mm});
            skLineSegment(sketch, "E226", {"start": v(-4.5, 0) * mm, "end": v(-4.5, 0) * mm});
            skCircle(sketch, "E227", {"center": v(-7, 0) * mm, "radius": 3 * mm});
            skCircle(sketch, "E228", {"center": v(-7, 0) * mm, "radius": 2.25 * mm});
            skPoint(sketch, "E229.trimOffspring.end.orphan", {"position": v(-9.5, 0) * mm});
            skPoint(sketch, "E230.start.orphan", {"position": v(-9.25, 0) * mm});
            skLineSegment(sketch, "E231.bottom", {"start": v(-9.5, 0) * mm, "end": v(-9.25, 0) * mm});
            skLineSegment(sketch, "E231.top", {"start": v(-9.5, 0.01) * mm, "end": v(-9.25, 0.01) * mm});
            skLineSegment(sketch, "E231.left", {"start": v(-9.5, 0) * mm, "end": v(-9.5, 0.01) * mm});
            skLineSegment(sketch, "E231.right", {"start": v(-9.25, 0) * mm, "end": v(-9.25, 0.01) * mm});
            skLineSegment(sketch, "E232.top", {"start": v(-9.5, -0.01) * mm, "end": v(-9.25, -0.01) * mm});
            skLineSegment(sketch, "E232.left", {"start": v(-9.5, 0) * mm, "end": v(-9.5, -0.01) * mm});
            skLineSegment(sketch, "E232.right", {"start": v(-9.25, 0) * mm, "end": v(-9.25, -0.01) * mm});
            skLineSegment(sketch, "E233.bottom", {"start": v(-4.5, 0) * mm, "end": v(-4.75, 0) * mm});
            skLineSegment(sketch, "E233.top", {"start": v(-4.5, 0.01) * mm, "end": v(-4.75, 0.01) * mm});
            skLineSegment(sketch, "E233.left", {"start": v(-4.5, 0) * mm, "end": v(-4.5, 0.01) * mm});
            skLineSegment(sketch, "E233.right", {"start": v(-4.75, 0) * mm, "end": v(-4.75, 0.01) * mm});
            skLineSegment(sketch, "E234.top", {"start": v(-4.5, -0.01) * mm, "end": v(-4.75, -0.01) * mm});
            skLineSegment(sketch, "E234.left", {"start": v(-4.5, 0) * mm, "end": v(-4.5, -0.01) * mm});
            skLineSegment(sketch, "E234.right", {"start": v(-4.75, 0) * mm, "end": v(-4.75, -0.01) * mm});
            skSolve(sketch);
        }
        {
            var Q0;
            Q0=makeQuery(id+"F22.imprint","IMPRINT",FACE,{"disambiguationData":[TD([[makeQuery(id+"F22.imprint","IMPRINT",EDGE,{"derivedFrom":sQuery(id+"F22.wireOp",EDGE,"E228")}),-1.0]])]});
            extrude(context, id + "F23", {"entities" : qUnion([Q0]), "oppositeDirection" : true, "depth" : 23 * mm});
        }
        {
            var Q0;
            Q0 = qSketchRegion(id + "F22", true);
            extrude(context, id + "F24", {"entities" : qUnion([Q0]), "oppositeDirection" : true, "depth" : 7 * mm});
        }
        {
            var Q0;
            Q0=makeQuery(id+"F22.imprint","IMPRINT",FACE,{"disambiguationData":[TD([[makeQuery(id+"F22.imprint","IMPRINT",EDGE,{"derivedFrom":sQuery(id+"F22.wireOp",EDGE,"E227")}),1.0]])]});
            extrude(context, id + "F25", {"entities" : qUnion([Q0]), "operationType" : NewBodyOperationType.REMOVE, "oppositeDirection" : true, "depth" : 6 * mm});
        }
        {
            var Q0;
            {var subQ1=sQuery(id+"F22.wireOp",EDGE,"E225");var subQ3=sQuery(id+"F22.wireOp",EDGE,"E231.top");var subQ4=makeQuery(id+"F22.imprint","INTERSECT",VERTEX,{"derivedFrom":[subQ1,subQ3]});Q0=makeQuery(id+"F22.imprint","IMPRINT",FACE,{"disambiguationData":[TD([[makeQuery(id+"F22.imprint","IMPRINT",EDGE,{"disambiguationData":[TD([[subQ4,-1.0]])],"derivedFrom":subQ1}),1.0]])]});}
            var Q1;
            {var subQ0=sQuery(id+"F22.wireOp",EDGE,"E231.bottom");var subQ5=sQuery(id+"F22.wireOp",EDGE,"E228");var subQ7=makeQuery(id+"F22.imprint","INTERSECT",VERTEX,{"derivedFrom":[subQ5,subQ0]});Q1=makeQuery(id+"F22.imprint","IMPRINT",FACE,{"disambiguationData":[TD([[makeQuery(id+"F22.imprint","IMPRINT",EDGE,{"disambiguationData":[TD([[subQ7,-1.0]])],"derivedFrom":subQ5}),-1.0]])]});}
            extrude(context, id + "F26", {"entities" : qUnion([Q0, Q1]), "operationType" : NewBodyOperationType.REMOVE, "oppositeDirection" : true, "depth" : 3 * mm});
        }
        {
            var Q0;
            {var subQ0=sQuery(id+"F22.wireOp",EDGE,"E233.bottom");var subQ5=sQuery(id+"F22.wireOp",EDGE,"E228");var subQ7=makeQuery(id+"F22.imprint","INTERSECT",VERTEX,{"derivedFrom":[subQ5,subQ0]});Q0=makeQuery(id+"F22.imprint","IMPRINT",FACE,{"disambiguationData":[TD([[makeQuery(id+"F22.imprint","IMPRINT",EDGE,{"disambiguationData":[TD([[subQ7,-1.0]])],"derivedFrom":subQ5}),-1.0]])]});}
            var Q1;
            {var subQ0=sQuery(id+"F22.wireOp",EDGE,"E233.bottom");var subQ5=sQuery(id+"F22.wireOp",EDGE,"E228");var subQ7=makeQuery(id+"F22.imprint","INTERSECT",VERTEX,{"derivedFrom":[subQ5,subQ0]});Q1=makeQuery(id+"F22.imprint","IMPRINT",FACE,{"disambiguationData":[TD([[makeQuery(id+"F22.imprint","IMPRINT",EDGE,{"disambiguationData":[TD([[subQ7,1.0]])],"derivedFrom":subQ5}),-1.0]])]});}
            extrude(context, id + "F27", {"entities" : qUnion([Q0, Q1]), "operationType" : NewBodyOperationType.REMOVE, "oppositeDirection" : true, "depth" : 3 * mm});
        }
    });
